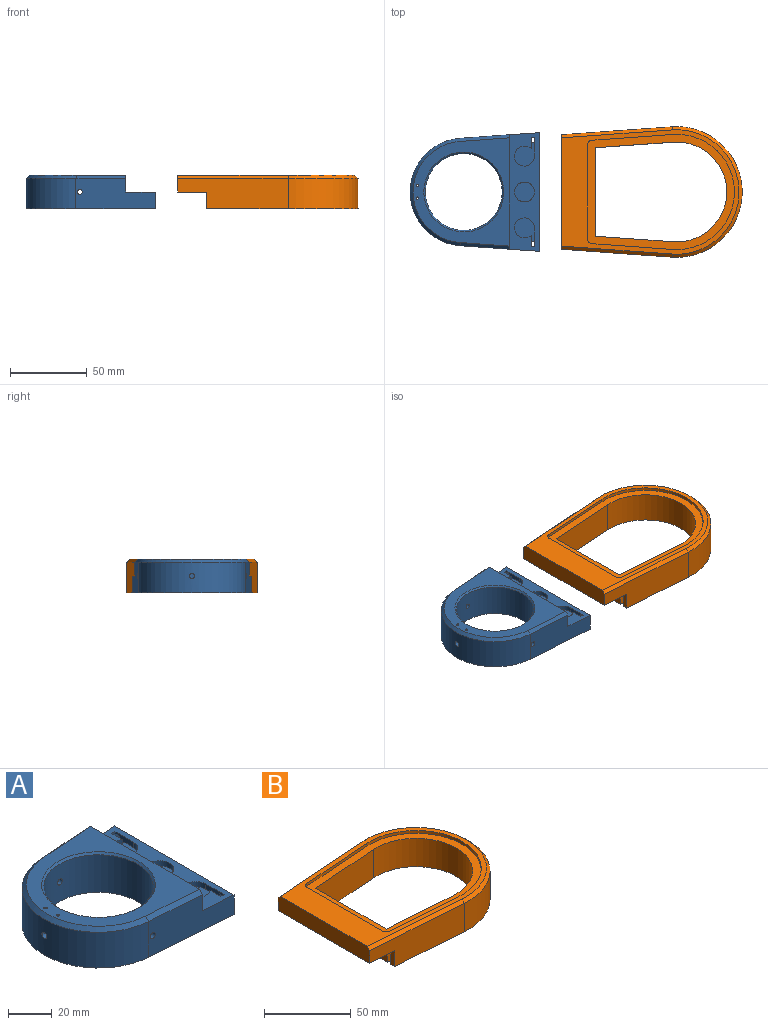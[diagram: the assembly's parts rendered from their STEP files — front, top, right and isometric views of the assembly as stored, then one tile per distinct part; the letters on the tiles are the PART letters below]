
ASSEMBLY  parts=2 mates=1
PART A: 41 faces, bbox 84x77.2x22 mm
  f0: plane 42.57x6.06mm, normal (0,0,-1), area 128mm2, adj f28,f29,f34,f40
  f1: plane 3.22x3mm, normal (0,0,-1), area 9mm2, adj f5,f10,f26,f37
  f2: plane 77.2x19mm, normal (0,0,1), area 1005.3mm2, adj f3,f4,f10,f13,f16,f17,f19,f26
  f3: cylinder r=6.5mm len=13mm, axis (0,0,-1), area 106.1mm2, adj f2,f21,f39,f40
  f4: cylinder r=6.5mm len=13mm, axis (0,0,-1), area 106.1mm2, adj f2,f22,f37,f38
  f5: plane 53.14x10.01mm, normal (-0.07,-1,0), area 527.2mm2, adj f1,f8,f10,f12,f22,f30,f31,f33
  f6: plane 70.47x63mm, normal (0,0,1), area 1633mm2, adj f13,f14,f23,f24,f25,f35,f36
  f7: plane 3.22x3mm, normal (0,0,-1), area 9mm2, adj f10,f28,f29,f39
  f8: plane 42.57x6.06mm, normal (0,0,-1), area 128mm2, adj f5,f26,f33,f38
  f9: plane 30.74x30.71mm, normal (0,0,-1), area 134.2mm2, adj f27,f28,f29,f30,f32,f34,f36
  f10: plane 77.2x11mm, normal (1,0,0), area 789mm2, adj f1,f2,f5,f7,f11,f12,f16,f17
  f11: plane 84x77.2mm, normal (0,0,-1), area 609.3mm2, adj f10,f16,f17,f18,f26,f27,f28
  f12: plane 78x65.17mm, normal (0,0,-1), area 2381.1mm2, adj f5,f10,f15,f29,f30
  f13: plane 74.48x11mm, normal (1,0,0), area 815.2mm2, adj f2,f6,f16,f17,f23,f25
  f14: cone r=25mm half-angle=45deg, axis (0,0,1), area 226.6mm2, adj f6,f15
  f15: cylinder r=25mm len=50mm, axis (0,0,-1), area 3274.5mm2, adj f12,f14,f32,f33,f34
  f16: plane 51.55x20.05mm, normal (-0.07,-1,0), area 853.1mm2, adj f2,f10,f11,f13,f18,f25,f33
  f17: plane 51.55x20.05mm, normal (-0.07,1,0), area 853.1mm2, adj f2,f10,f11,f13,f18,f23,f34
  f18: cylinder r=35mm len=69.82mm, axis (0,0,-1), area 2091mm2, adj f11,f16,f17,f24,f32
  f19: cylinder r=6.5mm len=13mm, axis (0,0,-1), area 122.5mm2, adj f2,f20
  f20: plane 13x13mm, normal (0,0,1), area 132.7mm2, adj f19
  f21: plane 15.51x13mm, normal (0,0,1), area 144.9mm2, adj f3,f29,f39,f40
  f22: plane 15.51x13mm, normal (0,0,1), area 144.9mm2, adj f4,f5,f37,f38
  f23: plane 32.5x4.32mm, normal (-0.05,0.71,0.71), area 92mm2, adj f6,f13,f17,f24
  f24: cone r=33mm half-angle=45deg, axis (0,0,-1), area 288.4mm2, adj f6,f18,f23,f25
  f25: plane 32.5x4.32mm, normal (-0.05,-0.71,0.71), area 92mm2, adj f6,f13,f16,f24
  f26: plane 53.14x11.01mm, normal (0.07,1,0), area 533.8mm2, adj f1,f2,f8,f10,f11,f27,f31,f33
  f27: cylinder r=32.07mm len=63.55mm, axis (0,0,-1), area 919mm2, adj f9,f11,f26,f28,f31,f32
  f28: plane 53.44x11.01mm, normal (0.07,-1,0), area 536.8mm2, adj f0,f2,f7,f9,f10,f11,f27,f34
  f29: plane 53.14x10.01mm, normal (-0.07,1,0), area 527.2mm2, adj f0,f7,f9,f10,f12,f21,f30,f34
  f30: cylinder r=29.09mm len=57.56mm, axis (0,0,-1), area 828.1mm2, adj f5,f9,f12,f29,f31,f32
  f31: plane 30.74x30.71mm, normal (0,0,-1), area 133.7mm2, adj f5,f26,f27,f30,f32,f33,f35
  f32: cylinder r=1.6mm len=10.05mm, axis (1,0,0), area 92mm2, adj f9,f15,f18,f27,f30,f31
  f33: cylinder r=1.6mm len=10.26mm, axis (0,-1,0), area 93mm2, adj f5,f8,f15,f16,f26,f31
  f34: cylinder r=1.6mm len=10.26mm, axis (0,-1,0), area 93.1mm2, adj f0,f9,f15,f17,f28,f29
  f35: cylinder r=0.75mm len=12mm, axis (0,0,1), area 56.5mm2, adj f6,f31
  f36: cylinder r=0.75mm len=12mm, axis (0,0,1), area 56.5mm2, adj f6,f9
  f37: plane 12.02x3mm, normal (-1,0,0), area 30mm2, adj f1,f2,f4,f5,f22,f26
  f38: plane 7x3mm, normal (1,0,0), area 15mm2, adj f2,f4,f5,f8,f22,f26
  f39: plane 12.02x3mm, normal (-1,0,0), area 30mm2, adj f2,f3,f7,f21,f28,f29
  f40: plane 7x3mm, normal (1,0,0), area 15mm2, adj f0,f2,f3,f21,f28,f29
PART B: 47 faces, bbox 117.5x85x22 mm
  f0: plane 65.17x14mm, normal (-1,0,0), area 717.5mm2, adj f4,f19,f23,f25,f32,f34,f37,f38
  f1: cylinder r=6.5mm len=13mm, axis (0,0,-1), area 110.1mm2, adj f4,f23,f39,f40
  f2: plane 98.5x85mm, normal (0,0,-1), area 723.2mm2, adj f3,f10,f11,f12,f20,f29,f30,f31
  f3: plane 11x3.01mm, normal (-1,0,0), area 33.1mm2, adj f2,f4,f10,f29
  f4: plane 114.5x79mm, normal (0,0,-1), area 1717.8mm2, adj f0,f1,f3,f10,f11,f18,f20,f21
  f5: plane 57.58x20mm, normal (1,0,0), area 1149.5mm2, adj f6,f8,f16,f19,f23,f25,f41,f42
  f6: plane 50.68x20mm, normal (0.07,-1,0), area 1010.2mm2, adj f5,f7,f16,f19,f23,f45,f46
  f7: cylinder r=32.5mm len=65mm, axis (0,0,-1), area 2135mm2, adj f6,f8,f16,f19
  f8: plane 50.68x20mm, normal (0.07,1,0), area 1010.2mm2, adj f5,f7,f16,f19,f25,f42,f43
  f9: plane 115.5x81mm, normal (0,0,1), area 1938.3mm2, adj f13,f14,f15,f17,f18,f26,f27,f28
  f10: plane 71.96x20mm, normal (-0.07,1,0), area 1233.4mm2, adj f2,f3,f4,f12,f18,f28
  f11: plane 71.96x20mm, normal (-0.07,-1,0), area 1233.4mm2, adj f2,f4,f12,f18,f20,f26
  f12: cylinder r=42.5mm len=85mm, axis (0,0,-1), area 2791.9mm2, adj f2,f10,f11,f27
  f13: plane 52.54x3.76mm, normal (0.07,1,0), area 105.3mm2, adj f9,f14,f16,f35
  f14: cylinder r=37.5mm len=75mm, axis (0,0,1), area 246.3mm2, adj f9,f13,f15,f16
  f15: plane 52.54x3.76mm, normal (0.07,-1,0), area 105.3mm2, adj f9,f14,f16,f36
  f16: plane 95.5x75mm, normal (0,0,1), area 1414mm2, adj f5,f6,f7,f8,f13,f14,f15,f17
  f17: plane 61.3x2mm, normal (1,0,0), area 122.6mm2, adj f9,f16,f35,f36
  f18: plane 74.48x11mm, normal (-1,0,0), area 815.2mm2, adj f4,f9,f10,f11,f26,f28
  f19: plane 92.5x73mm, normal (0,0,-1), area 1054.7mm2, adj f0,f5,f6,f7,f8,f32,f33,f34
  f20: plane 11x3.01mm, normal (-1,0,0), area 33.1mm2, adj f2,f4,f11,f31
  f21: cylinder r=6.5mm len=13mm, axis (0,0,-1), area 122.5mm2, adj f4,f22
  f22: plane 13x13mm, normal (0,0,-1), area 132.7mm2, adj f21
  f23: plane 21x13mm, normal (0,0,-1), area 148.9mm2, adj f0,f1,f5,f6,f39,f40,f44,f46
  f24: cylinder r=6.5mm len=13mm, axis (0,0,-1), area 110.1mm2, adj f4,f25,f37,f38
  f25: plane 21x13mm, normal (0,0,-1), area 148.9mm2, adj f0,f5,f8,f24,f37,f38,f41,f43
  f26: plane 72.11x7.16mm, normal (-0.05,-0.71,0.71), area 204.3mm2, adj f9,f11,f18,f27
  f27: cone r=40.5mm half-angle=45deg, axis (0,0,-1), area 385.5mm2, adj f9,f12,f26,f28
  f28: plane 72.11x7.16mm, normal (-0.05,0.71,0.71), area 204.3mm2, adj f9,f10,f18,f27
  f29: plane 53.18x11mm, normal (0.07,-1,0), area 586.5mm2, adj f2,f3,f4,f30
  f30: cylinder r=39.5mm len=79mm, axis (0,0,-1), area 1427.1mm2, adj f2,f4,f29,f31
  f31: plane 53.18x11mm, normal (0.07,1,0), area 586.5mm2, adj f2,f4,f20,f30
  f32: plane 53.39x11mm, normal (-0.07,-1,0), area 588.8mm2, adj f0,f4,f19,f33
  f33: cylinder r=36.5mm len=73mm, axis (0,0,-1), area 1318.8mm2, adj f4,f19,f32,f34
  f34: plane 53.39x11mm, normal (-0.07,1,0), area 588.8mm2, adj f0,f4,f19,f33
  f35: cylinder r=3mm len=2.99mm, axis (0,0,1), area 9mm2, adj f9,f13,f16,f17
  f36: cylinder r=3mm len=2.99mm, axis (0,0,-1), area 9mm2, adj f9,f15,f16,f17
  f37: plane 5.33x3mm, normal (0,-1,0), area 16mm2, adj f0,f4,f24,f25
  f38: plane 14.11x3mm, normal (0,1,0), area 42.1mm2, adj f0,f4,f24,f25,f42,f43
  f39: plane 5.33x3mm, normal (0,1,0), area 16mm2, adj f0,f1,f4,f23
  f40: plane 14.11x3mm, normal (0,-1,0), area 42.1mm2, adj f0,f1,f4,f23,f45,f46
  f41: plane 3x2.95mm, normal (0,-1,0), area 8.9mm2, adj f0,f5,f25,f42
  f42: plane 5x1.41mm, normal (0,0,1), area 6.2mm2, adj f0,f5,f8,f38,f41,f43
  f43: plane 2.95x0.92mm, normal (-1,0,0), area 2.7mm2, adj f8,f25,f38,f42
  f44: plane 3x2.95mm, normal (0,1,0), area 8.9mm2, adj f0,f5,f23,f45
  f45: plane 5x1.41mm, normal (0,0,1), area 6.2mm2, adj f0,f5,f6,f40,f44,f46
  f46: plane 2.95x0.92mm, normal (-1,0,0), area 2.7mm2, adj f6,f23,f40,f45
PLACE A t=(0,0,11)mm
PLACE B t=(33.6,0,11)mm
MATE slider B.f18 <-> A.f13  axis (-1,0,0) through (63.6,37.24,11)mm
